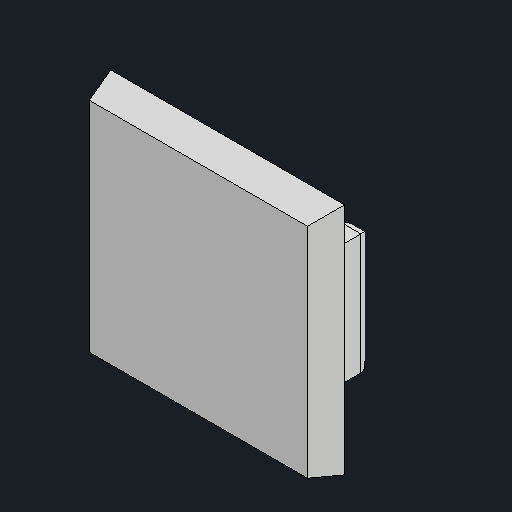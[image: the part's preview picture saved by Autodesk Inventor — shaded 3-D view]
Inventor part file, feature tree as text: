
AUTODESK INVENTOR PART (.ipt)
format: ipt  version: 2024.2 (Build 282272000, 272)  size: 167,424 bytes
history: native  units: mm
features: other x1, mirror x1
ambient origin geometry x8: Origin, YZ Plane, XZ Plane, XY Plane, X Axis, Y Axis, Z Axis, Center Point
bodies: Body1 (feature_tree)
feature tree (2):
  other  "솔리드1"
  mirror  "Mirror1"
